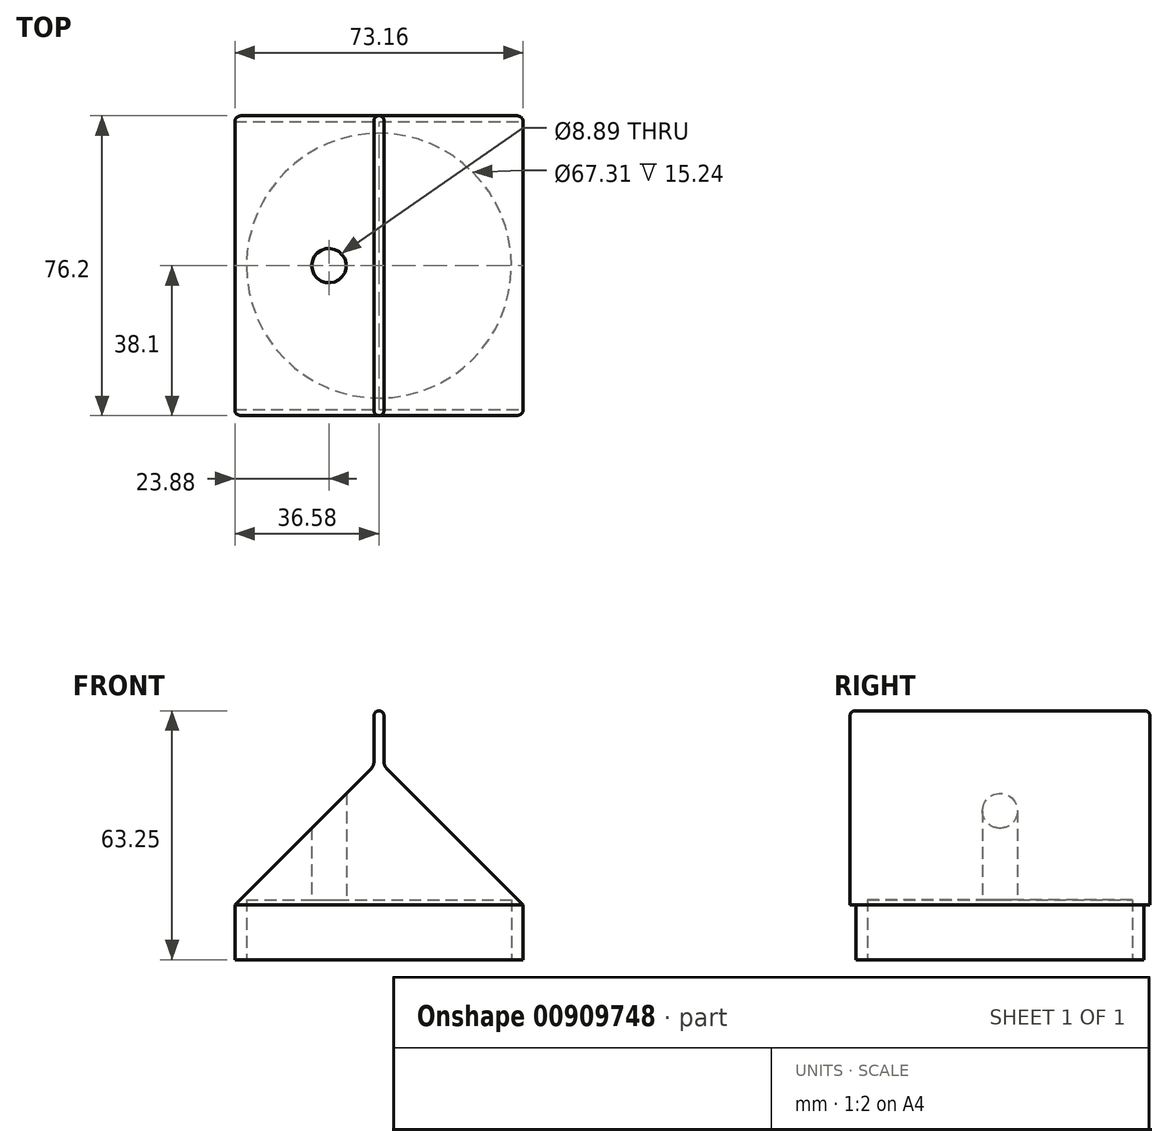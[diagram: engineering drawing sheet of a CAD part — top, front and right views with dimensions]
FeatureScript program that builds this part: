
annotation { "Feature Type Name" : "Feature", "Feature Type Description" : "" }
export const myFeature = defineFeature(function(context is Context, id is Id, definition is map)
    precondition{}
    {
        {
            var Q0;
            Q0=qCreatedBy(makeId("Front.planeOp"),FACE);
            var sketch = newSketch(context, id + "F0", { "sketchPlane" : qUnion([Q0])});
            skLineSegment(sketch, "E0.top", {"start": v(-36.58, -6.99) * mm, "end": v(36.58, -6.99) * mm});
            skLineSegment(sketch, "E0.left", {"start": v(-36.58, 6.99) * mm, "end": v(-36.58, -6.99) * mm});
            skLineSegment(sketch, "E0.right", {"start": v(36.58, 6.99) * mm, "end": v(36.58, -6.99) * mm});
            skPoint(sketch, "E0.middle", {"position": v(0, 0) * mm});
            skLineSegment(sketch, "E1", {"start": v(0, 56.26) * mm, "end": v(-1.27, 56.26) * mm});
            skLineSegment(sketch, "E2", {"start": v(0, 56.26) * mm, "end": v(1.27, 56.26) * mm});
            skLineSegment(sketch, "E3", {"start": v(1.27, 56.26) * mm, "end": v(1.27, 42.3) * mm});
            skLineSegment(sketch, "E4", {"start": v(-1.27, 56.26) * mm, "end": v(-1.27, 42.3) * mm});
            skLineSegment(sketch, "E5", {"start": v(-36.58, 6.99) * mm, "end": v(-1.27, 42.3) * mm});
            skLineSegment(sketch, "E6", {"start": v(1.27, 42.3) * mm, "end": v(36.58, 6.99) * mm});
            skSolve(sketch);
        }
        {
            var Q0;
            Q0=makeQuery(id+"F0.imprint","IMPRINT",FACE,{"disambiguationData":[TD([[makeQuery(id+"F0.imprint","IMPRINT",EDGE,{"derivedFrom":sQuery(id+"F0.wireOp",EDGE,"E0.top")}),1.0]])]});
            extrude(context, id + "F1", {"entities" : qUnion([Q0]), "endBound" : BoundingType.SYMMETRIC, "depth" : 76.2 * mm, "offsetDistance" : 25.4 * mm});
        }
        {
            var Q0;
            Q0=makeQuery(id+"F1.opExtrude","SWEPT_FACE",FACE,{"disambiguationData":[OSD([sQuery(id+"F0.wireOp",EDGE,"E0.top")])]});
            var sketch = newSketch(context, id + "F2", { "sketchPlane" : qUnion([Q0])});
            skLineSegment(sketch, "E7", {"start": v(-36.58, 36.58) * mm, "end": v(36.58, 36.58) * mm});
            skLineSegment(sketch, "E8", {"start": v(-36.58, -36.58) * mm, "end": v(36.58, -36.58) * mm});
            skSolve(sketch);
        }
        {
            var Q0;
            {var subQ0=sQuery(id+"F2.wireOp",EDGE,"E7");Q0=makeQuery(id+"F2.imprint","IMPRINT",FACE,{"disambiguationData":[TD([[makeQuery(id+"F2.imprint","IMPRINT",EDGE,{"derivedFrom":subQ0}),1.0]])]});}
            var Q1;
            {var subQ0=sQuery(id+"F2.wireOp",EDGE,"E8");Q1=makeQuery(id+"F2.imprint","IMPRINT",FACE,{"disambiguationData":[TD([[makeQuery(id+"F2.imprint","IMPRINT",EDGE,{"derivedFrom":subQ0}),-1.0]])]});}
            extrude(context, id + "F3", {"entities" : qUnion([Q0, Q1]), "operationType" : NewBodyOperationType.REMOVE, "oppositeDirection" : true, "depth" : 13.97 * mm, "offsetDistance" : 25.4 * mm});
        }
        {
            var Q0;
            Q0=makeQuery(id+"F1.opExtrude","SWEPT_FACE",FACE,{"disambiguationData":[OSD([sQuery(id+"F0.wireOp",EDGE,"E0.top")])]});
            var sketch = newSketch(context, id + "F4", { "sketchPlane" : qUnion([Q0])});
            skCircle(sketch, "E9", {"center": v(-12.7, 0) * mm, "radius": 4.44 * mm});
            skSolve(sketch);
        }
        {
            var Q0;
            Q0=makeQuery(id+"F4.imprint","IMPRINT",FACE,{"disambiguationData":[TD([[makeQuery(id+"F4.imprint","IMPRINT",EDGE,{"derivedFrom":sQuery(id+"F4.wireOp",EDGE,"E9")}),1.0]])]});
            extrude(context, id + "F5", {"entities" : qUnion([Q0]), "operationType" : NewBodyOperationType.REMOVE, "oppositeDirection" : true, "depth" : 76.2 * mm, "offsetDistance" : 25.4 * mm});
        }
        {
            var Q0;
            Q0=makeQuery(id+"F1.opExtrude","SWEPT_FACE",FACE,{"disambiguationData":[OSD([sQuery(id+"F0.wireOp",EDGE,"E0.top")])]});
            var sketch = newSketch(context, id + "F6", { "sketchPlane" : qUnion([Q0])});
            skCircle(sketch, "E10", {"center": v(0, 0) * mm, "radius": 33.66 * mm});
            skSolve(sketch);
        }
        {
            var Q0;
            Q0=makeQuery(id+"F6.imprint","IMPRINT",FACE,{"disambiguationData":[TD([[makeQuery(id+"F6.imprint","IMPRINT",EDGE,{"derivedFrom":sQuery(id+"F6.wireOp",EDGE,"E10")}),1.0]])]});
            extrude(context, id + "F7", {"entities" : qUnion([Q0]), "operationType" : NewBodyOperationType.REMOVE, "oppositeDirection" : true, "depth" : 15.24 * mm, "offsetDistance" : 25.4 * mm});
        }
        {
            var Q0;
            Q0=makeQuery(id+"F1.opExtrude","SWEPT_EDGE",EDGE,{"disambiguationData":[OSD([sQuery(id+"F0.wireOp",EDGE,"E4"),sQuery(id+"F0.wireOp",EDGE,"E5")])]});
            var Q1;
            Q1=makeQuery(id+"F1.opExtrude","SWEPT_EDGE",EDGE,{"disambiguationData":[OSD([sQuery(id+"F0.wireOp",EDGE,"E3"),sQuery(id+"F0.wireOp",EDGE,"E6")])]});
            fillet(context, id + "F8", {"entities" : qUnion([Q0, Q1]), "radius" : 2.54 * mm, "tangentPropagation" : true, "allowEdgeOverflow" : false});
        }
        {
            var Q0;
            Q0=makeQuery(id+"F1.opExtrude","SWEPT_FACE",FACE,{"disambiguationData":[OSD([sQuery(id+"F0.wireOp",EDGE,"E1"),sQuery(id+"F0.wireOp",EDGE,"E2")])]});
            var Q1;
            Q1=makeQuery(id+"F1.opExtrude","CAP_EDGE",EDGE,{"disambiguationData":[OSD([sQuery(id+"F0.wireOp",EDGE,"E4")])],"isStart":false});
            var Q2;
            Q2=makeQuery(id+"F1.opExtrude","CAP_EDGE",EDGE,{"disambiguationData":[OSD([sQuery(id+"F0.wireOp",EDGE,"E6")])],"isStart":false});
            var Q3;
            Q3=makeQuery(id+"F1.opExtrude","CAP_EDGE",EDGE,{"disambiguationData":[OSD([sQuery(id+"F0.wireOp",EDGE,"E3")])],"isStart":false});
            var Q4;
            Q4=makeQuery(id+"F1.opExtrude","CAP_EDGE",EDGE,{"disambiguationData":[OSD([sQuery(id+"F0.wireOp",EDGE,"E4")])],"isStart":true});
            var Q5;
            Q5=makeQuery(id+"F1.opExtrude","CAP_EDGE",EDGE,{"disambiguationData":[OSD([sQuery(id+"F0.wireOp",EDGE,"E3")])],"isStart":true});
            fillet(context, id + "F9", {"entities" : qUnion([Q0, Q1, Q2, Q3, Q4, Q5]), "radius" : 1.27 * mm, "tangentPropagation" : true, "allowEdgeOverflow" : false});
        }
    });
